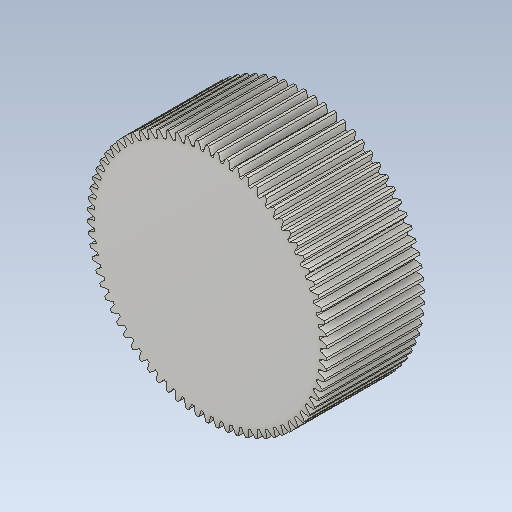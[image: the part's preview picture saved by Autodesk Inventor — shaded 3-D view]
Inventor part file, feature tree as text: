
AUTODESK INVENTOR PART (.ipt)
format: ipt  version: 2021 (Build 250183000, 183)  size: 477,184 bytes
history: native  units: mm (DEFAULTED — no unit token found)
features: plane x3, other x3, sketch x2, extrude x1
ambient origin geometry x8: Origin, YZ Plane, XZ Plane, XY Plane, X Axis, Y Axis, Z Axis, Center Point
bodies: Solid1 (feature_tree)
feature tree (9):
  extrude  "Extrusion1"  Depth=5.0mm TaperAngle=0.0deg
  plane  "Work Plane2"
  plane  "Work Plane8"
  plane  "Work Plane9"
  other  "Spur Gear"
  sketch  "Sketch1"  dims[d0=12.28mm d1=5.0mm d2=0.0mm]
  sketch  "Sketch2"  dims[d3=11.84mm d4=10.0mm d5=0.0mm d16=7.5mm d17=0.0mm d34=0.42454mm d39=0.0mm d41=0.0mm d43=7.5mm d46=7.5mm d47=0.0mm d48=0.0mm]
  other  "Srf1"
  other  "Pitch Diameter"
